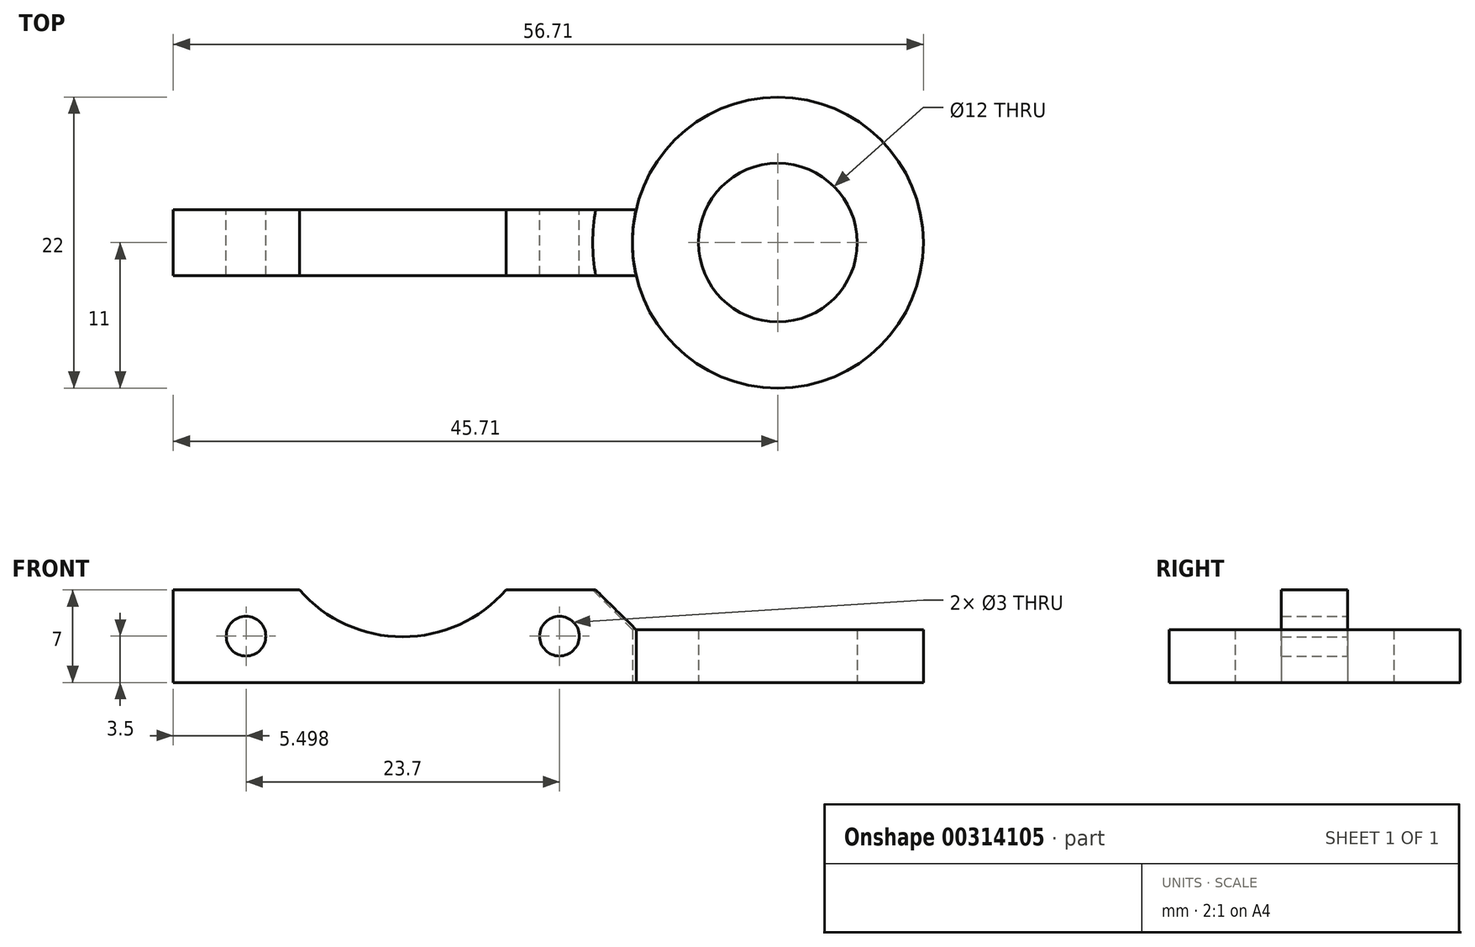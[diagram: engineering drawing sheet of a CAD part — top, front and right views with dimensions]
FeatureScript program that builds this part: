
annotation { "Feature Type Name" : "Feature", "Feature Type Description" : "" }
export const myFeature = defineFeature(function(context is Context, id is Id, definition is map)
    precondition{}
    {
        {
            var Q0;
            Q0=qCreatedBy(makeId("Top.planeOp"),FACE);
            var sketch = newSketch(context, id + "F0", { "sketchPlane" : qUnion([Q0])});
            skCircle(sketch, "E0", {"center": v(0, 0) * mm, "radius": 6 * mm});
            skCircle(sketch, "E1.0", {"center": v(0, 0) * mm, "radius": 11 * mm});
            skLineSegment(sketch, "E2.bottom", {"start": v(-45.71, -2.5) * mm, "end": v(-10.71, -2.5) * mm});
            skLineSegment(sketch, "E3.MirrorCS", {"start": v(-45.71, 2.5) * mm, "end": v(-10.71, 2.5) * mm});
            skLineSegment(sketch, "E4", {"start": v(-45.71, 2.5) * mm, "end": v(-45.71, -2.5) * mm});
            skLineSegment(sketch, "E5.0", {"start": v(-41.71, 2.5) * mm, "end": v(-41.71, -2.5) * mm});
            skLineSegment(sketch, "E6.0", {"start": v(-40.21, 2.5) * mm, "end": v(-40.21, -2.5) * mm});
            skLineSegment(sketch, "E7.0", {"start": v(-38.71, 2.5) * mm, "end": v(-38.71, -2.5) * mm});
            skLineSegment(sketch, "E8.0", {"start": v(-16.51, 2.5) * mm, "end": v(-16.51, -2.5) * mm});
            skLineSegment(sketch, "E9.0", {"start": v(-18.01, 2.5) * mm, "end": v(-18.01, -2.5) * mm});
            skLineSegment(sketch, "E10.0", {"start": v(-15.01, 2.5) * mm, "end": v(-15.01, -2.5) * mm});
            skLineSegment(sketch, "E11.0", {"start": v(-28.36, 2.5) * mm, "end": v(-28.36, -2.5) * mm});
            skSolve(sketch);
        }
        {
            var Q0;
            Q0=makeQuery(id+"F0.imprint","IMPRINT",FACE,{"disambiguationData":[TD([[makeQuery(id+"F0.imprint","IMPRINT",EDGE,{"derivedFrom":sQuery(id+"F0.wireOp",EDGE,"E0")}),-1.0]])]});
            extrude(context, id + "F1", {"entities" : qUnion([Q0]), "depth" : 4 * mm});
        }
        {
            var Q0;
            {var subQ5=sQuery(id+"F0.wireOp",EDGE,"E10.0");Q0=makeQuery(id+"F0.imprint","IMPRINT",FACE,{"disambiguationData":[TD([[makeQuery(id+"F0.imprint","IMPRINT",EDGE,{"derivedFrom":subQ5}),1.0]])]});}
            var Q1;
            {var subQ0=sQuery(id+"F0.wireOp",EDGE,"E8.0");Q1=makeQuery(id+"F0.imprint","IMPRINT",FACE,{"disambiguationData":[TD([[makeQuery(id+"F0.imprint","IMPRINT",EDGE,{"derivedFrom":subQ0}),1.0]])]});}
            var Q2;
            {var subQ0=sQuery(id+"F0.wireOp",EDGE,"E8.0");Q2=makeQuery(id+"F0.imprint","IMPRINT",FACE,{"disambiguationData":[TD([[makeQuery(id+"F0.imprint","IMPRINT",EDGE,{"derivedFrom":subQ0}),-1.0]])]});}
            var Q3;
            {var subQ0=sQuery(id+"F0.wireOp",EDGE,"E7.0");Q3=makeQuery(id+"F0.imprint","IMPRINT",FACE,{"disambiguationData":[TD([[makeQuery(id+"F0.imprint","IMPRINT",EDGE,{"derivedFrom":subQ0}),1.0]])]});}
            var Q4;
            {var subQ0=sQuery(id+"F0.wireOp",EDGE,"E6.0");Q4=makeQuery(id+"F0.imprint","IMPRINT",FACE,{"disambiguationData":[TD([[makeQuery(id+"F0.imprint","IMPRINT",EDGE,{"derivedFrom":subQ0}),1.0]])]});}
            var Q5;
            {var subQ0=sQuery(id+"F0.wireOp",EDGE,"E5.0");Q5=makeQuery(id+"F0.imprint","IMPRINT",FACE,{"disambiguationData":[TD([[makeQuery(id+"F0.imprint","IMPRINT",EDGE,{"derivedFrom":subQ0}),1.0]])]});}
            var Q6;
            {var subQ0=sQuery(id+"F0.wireOp",EDGE,"E4");Q6=makeQuery(id+"F0.imprint","IMPRINT",FACE,{"disambiguationData":[TD([[makeQuery(id+"F0.imprint","IMPRINT",EDGE,{"derivedFrom":subQ0}),1.0]])]});}
            var Q7;
            {var subQ0=sQuery(id+"F0.wireOp",EDGE,"E9.0");Q7=makeQuery(id+"F0.imprint","IMPRINT",FACE,{"disambiguationData":[TD([[makeQuery(id+"F0.imprint","IMPRINT",EDGE,{"derivedFrom":subQ0}),-1.0]])]});}
            extrude(context, id + "F2", {"entities" : qUnion([Q0, Q1, Q2, Q3, Q4, Q5, Q6, Q7]), "depth" : 7 * mm});
        }
        {
            var Q0;
            {var subQ0=sQuery(id+"F0.wireOp",EDGE,"E8.0");Q0=makeQuery(id+"F0.imprint","IMPRINT",FACE,{"disambiguationData":[TD([[makeQuery(id+"F0.imprint","IMPRINT",EDGE,{"derivedFrom":subQ0}),1.0]])]});}
            var Q1;
            Q1=sQuery(id+"F0.wireOp",EDGE,"E8.0");
            revolve(context, id + "F3", {"entities" : qUnion([Q0]), "axis" : qUnion([Q1]), "revolveType" : RevolveType.FULL});
        }
        {
            var Q0;
            {var subQ0=sQuery(id+"F0.wireOp",EDGE,"E6.0");Q0=makeQuery(id+"F0.imprint","IMPRINT",FACE,{"disambiguationData":[TD([[makeQuery(id+"F0.imprint","IMPRINT",EDGE,{"derivedFrom":subQ0}),1.0]])]});}
            var Q1;
            Q1=sQuery(id+"F0.wireOp",EDGE,"E6.0");
            revolve(context, id + "F4", {"entities" : qUnion([Q0]), "axis" : qUnion([Q1]), "revolveType" : RevolveType.FULL});
        }
        {
            var Q0;
            Q0=makeQuery(id+"F4.opRevolve","SWEPT_BODY",BODY,{"disambiguationData":[OSD([sQuery(id+"F0.wireOp",EDGE,"E2.bottom"),sQuery(id+"F0.wireOp",EDGE,"E3.MirrorCS"),sQuery(id+"F0.wireOp",EDGE,"E6.0"),sQuery(id+"F0.wireOp",EDGE,"E7.0")])]});
            var Q1;
            Q1=makeQuery(id+"F3.opRevolve","SWEPT_BODY",BODY,{"disambiguationData":[OSD([sQuery(id+"F0.wireOp",EDGE,"E2.bottom"),sQuery(id+"F0.wireOp",EDGE,"E3.MirrorCS"),sQuery(id+"F0.wireOp",EDGE,"E8.0"),sQuery(id+"F0.wireOp",EDGE,"E10.0")])]});
            transform(context, id + "F5", {"entities" : qUnion([Q0, Q1]), "transformType" : TransformType.TRANSLATION_3D, "dx" : 0 * mm, "dy" : 0 * mm, "dz" : 3.5 * mm, "makeCopy" : false});
        }
        {
            var Q0;
            Q0=makeQuery(id+"F2.opExtrude","CAP_EDGE",EDGE,{"disambiguationData":[OSD([sQuery(id+"F0.wireOp",EDGE,"E1.0")])],"isStart":false});
            chamfer(context, id + "F6", {"entities" : qUnion([Q0]), "width" : 3 * mm, "tangentPropagation" : true});
        }
        {
            var Q0;
            {var subQ0=sQuery(id+"F0.wireOp",EDGE,"E9.0");Q0=makeQuery(id+"F0.imprint","IMPRINT",FACE,{"disambiguationData":[TD([[makeQuery(id+"F0.imprint","IMPRINT",EDGE,{"derivedFrom":subQ0}),-1.0]])]});}
            var Q1;
            Q1=sQuery(id+"F0.wireOp",EDGE,"E11.0");
            revolve(context, id + "F7", {"entities" : qUnion([Q0]), "axis" : qUnion([Q1]), "revolveType" : RevolveType.FULL});
        }
        {
            var Q0;
            Q0=makeQuery(id+"F7.opRevolve","SWEPT_BODY",BODY,{"disambiguationData":[OSD([sQuery(id+"F0.wireOp",EDGE,"E2.bottom"),sQuery(id+"F0.wireOp",EDGE,"E3.MirrorCS"),sQuery(id+"F0.wireOp",EDGE,"E9.0"),sQuery(id+"F0.wireOp",EDGE,"E11.0")])]});
            transform(context, id + "F8", {"entities" : qUnion([Q0]), "transformType" : TransformType.TRANSLATION_3D, "dx" : 0 * mm, "dy" : 0 * mm, "dz" : 13.8 * mm, "makeCopy" : false});
        }
        {
            var Q0;
            Q0=makeQuery(id+"F4.opRevolve","SWEPT_BODY",BODY,{"disambiguationData":[OSD([sQuery(id+"F0.wireOp",EDGE,"E2.bottom"),sQuery(id+"F0.wireOp",EDGE,"E3.MirrorCS"),sQuery(id+"F0.wireOp",EDGE,"E6.0"),sQuery(id+"F0.wireOp",EDGE,"E7.0")])]});
            var Q1;
            Q1=makeQuery(id+"F7.opRevolve","SWEPT_BODY",BODY,{"disambiguationData":[OSD([sQuery(id+"F0.wireOp",EDGE,"E2.bottom"),sQuery(id+"F0.wireOp",EDGE,"E3.MirrorCS"),sQuery(id+"F0.wireOp",EDGE,"E9.0"),sQuery(id+"F0.wireOp",EDGE,"E11.0")])]});
            var Q2;
            Q2=makeQuery(id+"F3.opRevolve","SWEPT_BODY",BODY,{"disambiguationData":[OSD([sQuery(id+"F0.wireOp",EDGE,"E2.bottom"),sQuery(id+"F0.wireOp",EDGE,"E3.MirrorCS"),sQuery(id+"F0.wireOp",EDGE,"E8.0"),sQuery(id+"F0.wireOp",EDGE,"E10.0")])]});
            var Q3;
            Q3=makeQuery(id+"F2.opExtrude","SWEPT_BODY",BODY,{"disambiguationData":[OSD([sQuery(id+"F0.wireOp",EDGE,"E1.0"),sQuery(id+"F0.wireOp",EDGE,"E2.bottom"),sQuery(id+"F0.wireOp",EDGE,"E3.MirrorCS"),sQuery(id+"F0.wireOp",EDGE,"E4")])]});
            booleanBodies(context, id + "F9", {"operationType" : BooleanOperationType.SUBTRACTION, "tools" : qUnion([Q0, Q1, Q2]), "targets" : qUnion([Q3])});
        }
    });
